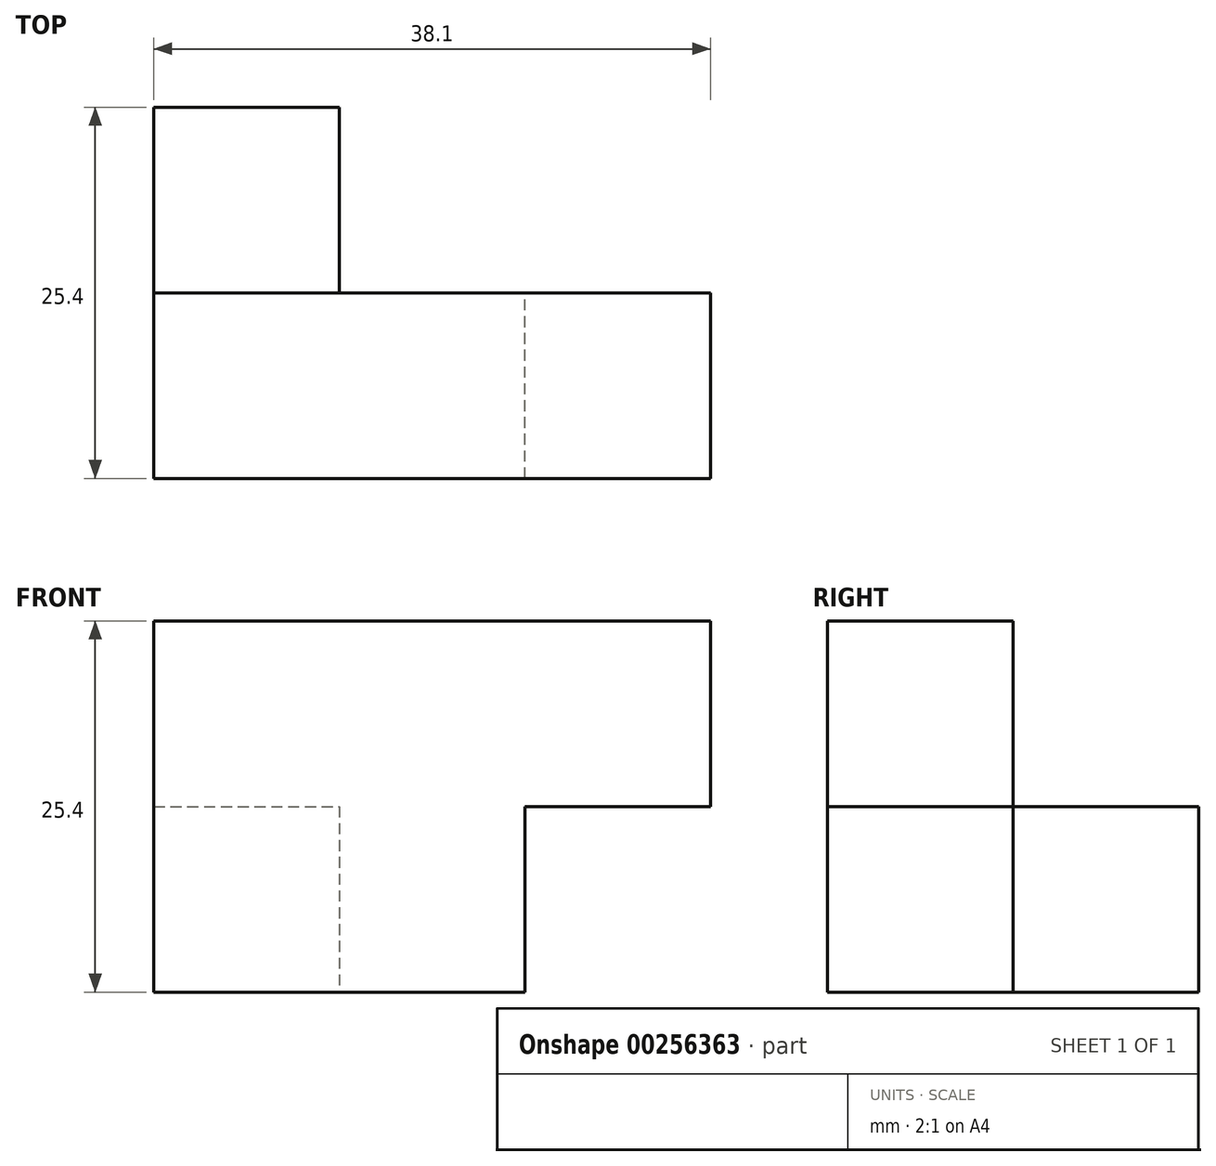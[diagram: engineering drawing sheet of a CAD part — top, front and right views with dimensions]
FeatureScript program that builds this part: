
annotation { "Feature Type Name" : "Feature", "Feature Type Description" : "" }
export const myFeature = defineFeature(function(context is Context, id is Id, definition is map)
    precondition{}
    {
        {
            var Q0;
            Q0=qCreatedBy(makeId("Front.planeOp"),FACE);
            var sketch = newSketch(context, id + "F0", { "sketchPlane" : qUnion([Q0])});
            skLineSegment(sketch, "E0", {"start": v(0, 0) * mm, "end": v(0, 25.4) * mm});
            skLineSegment(sketch, "E1", {"start": v(0, 25.4) * mm, "end": v(38.1, 25.4) * mm});
            skLineSegment(sketch, "E2", {"start": v(38.1, 25.4) * mm, "end": v(38.1, 12.7) * mm});
            skLineSegment(sketch, "E3", {"start": v(38.1, 12.7) * mm, "end": v(25.4, 12.7) * mm});
            skLineSegment(sketch, "E4", {"start": v(25.4, 12.7) * mm, "end": v(25.4, 0) * mm});
            skLineSegment(sketch, "E5", {"start": v(25.4, 0) * mm, "end": v(0, 0) * mm});
            skSolve(sketch);
        }
        {
            var Q0;
            Q0=makeQuery(id+"F0.imprint","IMPRINT",FACE,{"disambiguationData":[TD([[makeQuery(id+"F0.imprint","IMPRINT",EDGE,{"derivedFrom":sQuery(id+"F0.wireOp",EDGE,"E0")}),-1.0]])]});
            extrude(context, id + "F1", {"entities" : qUnion([Q0]), "depth" : 12.7 * mm});
        }
        {
            var Q0;
            Q0=makeQuery(id+"F1.opExtrude","CAP_FACE",FACE,{"disambiguationData":[OSD([sQuery(id+"F0.wireOp",EDGE,"E0"),sQuery(id+"F0.wireOp",EDGE,"E1"),sQuery(id+"F0.wireOp",EDGE,"E2"),sQuery(id+"F0.wireOp",EDGE,"E3"),sQuery(id+"F0.wireOp",EDGE,"E4"),sQuery(id+"F0.wireOp",EDGE,"E5")])],"isStart":true});
            var sketch = newSketch(context, id + "F2", { "sketchPlane" : qUnion([Q0])});
            skLineSegment(sketch, "E6", {"start": v(0, 12.7) * mm, "end": v(-12.7, 12.7) * mm});
            skLineSegment(sketch, "E7", {"start": v(-12.7, 12.7) * mm, "end": v(-12.7, 0) * mm});
            skLineSegment(sketch, "E8", {"start": v(-12.7, 0) * mm, "end": v(0, 0) * mm});
            skLineSegment(sketch, "E9", {"start": v(0, 0) * mm, "end": v(0, 12.7) * mm});
            skSolve(sketch);
        }
        {
            var Q0;
            Q0=makeQuery(id+"F2.imprint","IMPRINT",FACE,{"disambiguationData":[TD([[makeQuery(id+"F2.imprint","IMPRINT",EDGE,{"derivedFrom":sQuery(id+"F2.wireOp",EDGE,"E6")}),1.0]])]});
            extrude(context, id + "F3", {"entities" : qUnion([Q0]), "operationType" : NewBodyOperationType.ADD, "depth" : 12.7 * mm});
        }
    });
